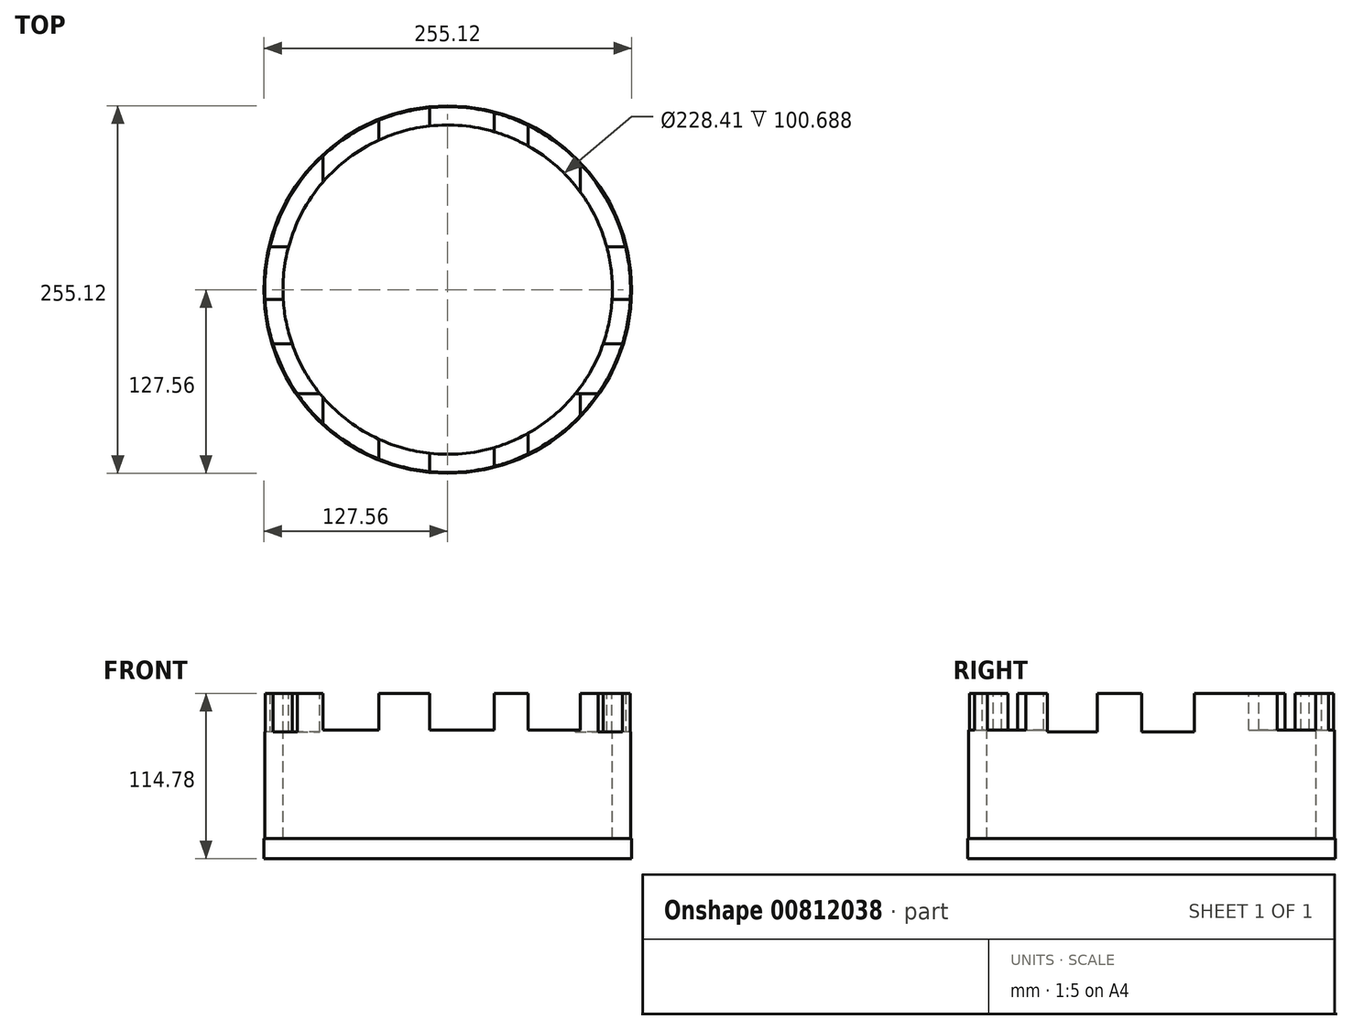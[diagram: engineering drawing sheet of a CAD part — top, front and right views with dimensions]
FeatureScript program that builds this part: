
annotation { "Feature Type Name" : "Feature", "Feature Type Description" : "" }
export const myFeature = defineFeature(function(context is Context, id is Id, definition is map)
    precondition{}
    {
        {
            var Q0;
            Q0=qCreatedBy(makeId("Top.planeOp"),FACE);
            var sketch = newSketch(context, id + "F0", { "sketchPlane" : qUnion([Q0])});
            skCircle(sketch, "E0", {"center": v(0, 0) * mm, "radius": 126.81 * mm});
            skSolve(sketch);
        }
        {
            var Q0;
            Q0 = qSketchRegion(id + "F0", true);
            extrude(context, id + "F1", {"entities" : qUnion([Q0]), "depth" : 100.69 * mm, "offsetDistance" : 25 * mm});
        }
        {
            var Q0;
            Q0=makeQuery(id+"F1.opExtrude","CAP_FACE",FACE,{"disambiguationData":[OSD([sQuery(id+"F0.wireOp",EDGE,"E0")])],"isStart":false});
            var sketch = newSketch(context, id + "F2", { "sketchPlane" : qUnion([Q0])});
            skCircle(sketch, "E1", {"center": v(0, 0) * mm, "radius": 114.2 * mm});
            skSolve(sketch);
        }
        {
            var Q0;
            Q0 = qSketchRegion(id + "F2", true);
            extrude(context, id + "F3", {"entities" : qUnion([Q0]), "operationType" : NewBodyOperationType.REMOVE, "oppositeDirection" : true, "depth" : 132.48 * mm, "offsetDistance" : 25 * mm});
        }
        {
            var Q0;
            Q0=qCreatedBy(makeId("Front.planeOp"),FACE);
            var sketch = newSketch(context, id + "F4", { "sketchPlane" : qUnion([Q0])});
            skLineSegment(sketch, "E2.bottom", {"start": v(-74.29, 75.03) * mm, "end": v(-55.32, 75.03) * mm});
            skLineSegment(sketch, "E2.top", {"start": v(-74.29, 57.55) * mm, "end": v(-55.32, 57.55) * mm});
            skLineSegment(sketch, "E2.left", {"start": v(-74.29, 75.03) * mm, "end": v(-74.29, 57.55) * mm});
            skLineSegment(sketch, "E2.right", {"start": v(-55.32, 75.03) * mm, "end": v(-55.32, 57.55) * mm});
            skSolve(sketch);
        }
        {
            var Q0;
            Q0 = qSketchRegion(id + "F4", true);
            extrude(context, id + "F5", {"entities" : qUnion([Q0]), "depth" : 25 * mm, "offsetDistance" : 25 * mm});
        }
        {
            var Q0;
            Q0=makeQuery(id+"F5.opExtrude","SWEPT_BODY",BODY,{"disambiguationData":[OSD([sQuery(id+"F4.wireOp",EDGE,"E2.bottom"),sQuery(id+"F4.wireOp",EDGE,"E2.top"),sQuery(id+"F4.wireOp",EDGE,"E2.left"),sQuery(id+"F4.wireOp",EDGE,"E2.right")])]});
            deleteBodies(context, id + "F6", {"entities" : qUnion([Q0])});
        }
        {
            var Q0;
            Q0=qCreatedBy(makeId("Right.planeOp"),FACE);
            var sketch = newSketch(context, id + "F7", { "sketchPlane" : qUnion([Q0])});
            skLineSegment(sketch, "E3.bottom", {"start": v(-72.11, 101.14) * mm, "end": v(-37.44, 101.14) * mm});
            skLineSegment(sketch, "E3.top", {"start": v(-72.11, 73.8) * mm, "end": v(-37.44, 73.8) * mm});
            skLineSegment(sketch, "E3.left", {"start": v(-72.11, 101.14) * mm, "end": v(-72.11, 73.8) * mm});
            skLineSegment(sketch, "E3.right", {"start": v(-37.44, 101.14) * mm, "end": v(-37.44, 73.8) * mm});
            skPoint(sketch, "E4.oppositeSnap0", {"position": v(-54.78, 73.8) * mm});
            skLineSegment(sketch, "E4.bottom", {"start": v(-6.91, 102.04) * mm, "end": v(29.59, 102.04) * mm});
            skLineSegment(sketch, "E4.top", {"start": v(-6.91, 73.8) * mm, "end": v(29.59, 73.8) * mm});
            skLineSegment(sketch, "E4.left", {"start": v(-6.91, 102.04) * mm, "end": v(-6.91, 73.8) * mm});
            skLineSegment(sketch, "E4.right", {"start": v(29.59, 102.04) * mm, "end": v(29.59, 73.8) * mm});
            skSolve(sketch);
        }
        {
            var Q0;
            Q0 = qSketchRegion(id + "F7", true);
            extrude(context, id + "F8", {"entities" : qUnion([Q0]), "operationType" : NewBodyOperationType.REMOVE, "endBound" : BoundingType.SYMMETRIC, "depth" : 326.56 * mm, "offsetDistance" : 25 * mm});
        }
        {
            var Q0;
            Q0=qCreatedBy(makeId("Front.planeOp"),FACE);
            var sketch = newSketch(context, id + "F9", { "sketchPlane" : qUnion([Q0])});
            skLineSegment(sketch, "E5.bottom", {"start": v(-86.5, 105.24) * mm, "end": v(-47.61, 105.24) * mm});
            skLineSegment(sketch, "E5.top", {"start": v(-86.5, 75.26) * mm, "end": v(-47.61, 75.26) * mm});
            skLineSegment(sketch, "E5.left", {"start": v(-86.5, 105.24) * mm, "end": v(-86.5, 75.26) * mm});
            skLineSegment(sketch, "E5.right", {"start": v(-47.61, 105.24) * mm, "end": v(-47.61, 75.26) * mm});
            skLineSegment(sketch, "E6.bottom", {"start": v(-12.48, 105.24) * mm, "end": v(32.37, 105.24) * mm});
            skLineSegment(sketch, "E6.top", {"start": v(-12.48, 75.26) * mm, "end": v(32.37, 75.26) * mm});
            skLineSegment(sketch, "E6.left", {"start": v(-12.48, 105.24) * mm, "end": v(-12.48, 75.26) * mm});
            skLineSegment(sketch, "E6.right", {"start": v(32.37, 105.24) * mm, "end": v(32.37, 75.26) * mm});
            skLineSegment(sketch, "E7.bottom", {"start": v(55.88, 105.24) * mm, "end": v(92.05, 105.24) * mm});
            skLineSegment(sketch, "E7.top", {"start": v(55.88, 75.26) * mm, "end": v(92.05, 75.26) * mm});
            skLineSegment(sketch, "E7.left", {"start": v(55.88, 105.24) * mm, "end": v(55.88, 75.26) * mm});
            skLineSegment(sketch, "E7.right", {"start": v(92.05, 105.24) * mm, "end": v(92.05, 75.26) * mm});
            skSolve(sketch);
        }
        {
            var Q0;
            Q0 = qSketchRegion(id + "F9", true);
            extrude(context, id + "F10", {"entities" : qUnion([Q0]), "operationType" : NewBodyOperationType.REMOVE, "endBound" : BoundingType.SYMMETRIC, "depth" : 425.5 * mm, "offsetDistance" : 25 * mm});
        }
        {
            var Q0;
            Q0 = qSketchRegion(id + "F0", true);
            var sketch = newSketch(context, id + "F11", { "sketchPlane" : qUnion([Q0])});
            skCircle(sketch, "E8", {"center": v(0, 0) * mm, "radius": 127.56 * mm});
            skSolve(sketch);
        }
        {
            var Q0;
            Q0 = qSketchRegion(id + "F11", true);
            extrude(context, id + "F12", {"entities" : qUnion([Q0]), "operationType" : NewBodyOperationType.ADD, "oppositeDirection" : true, "depth" : 14.1 * mm, "offsetDistance" : 25 * mm});
        }
    });
